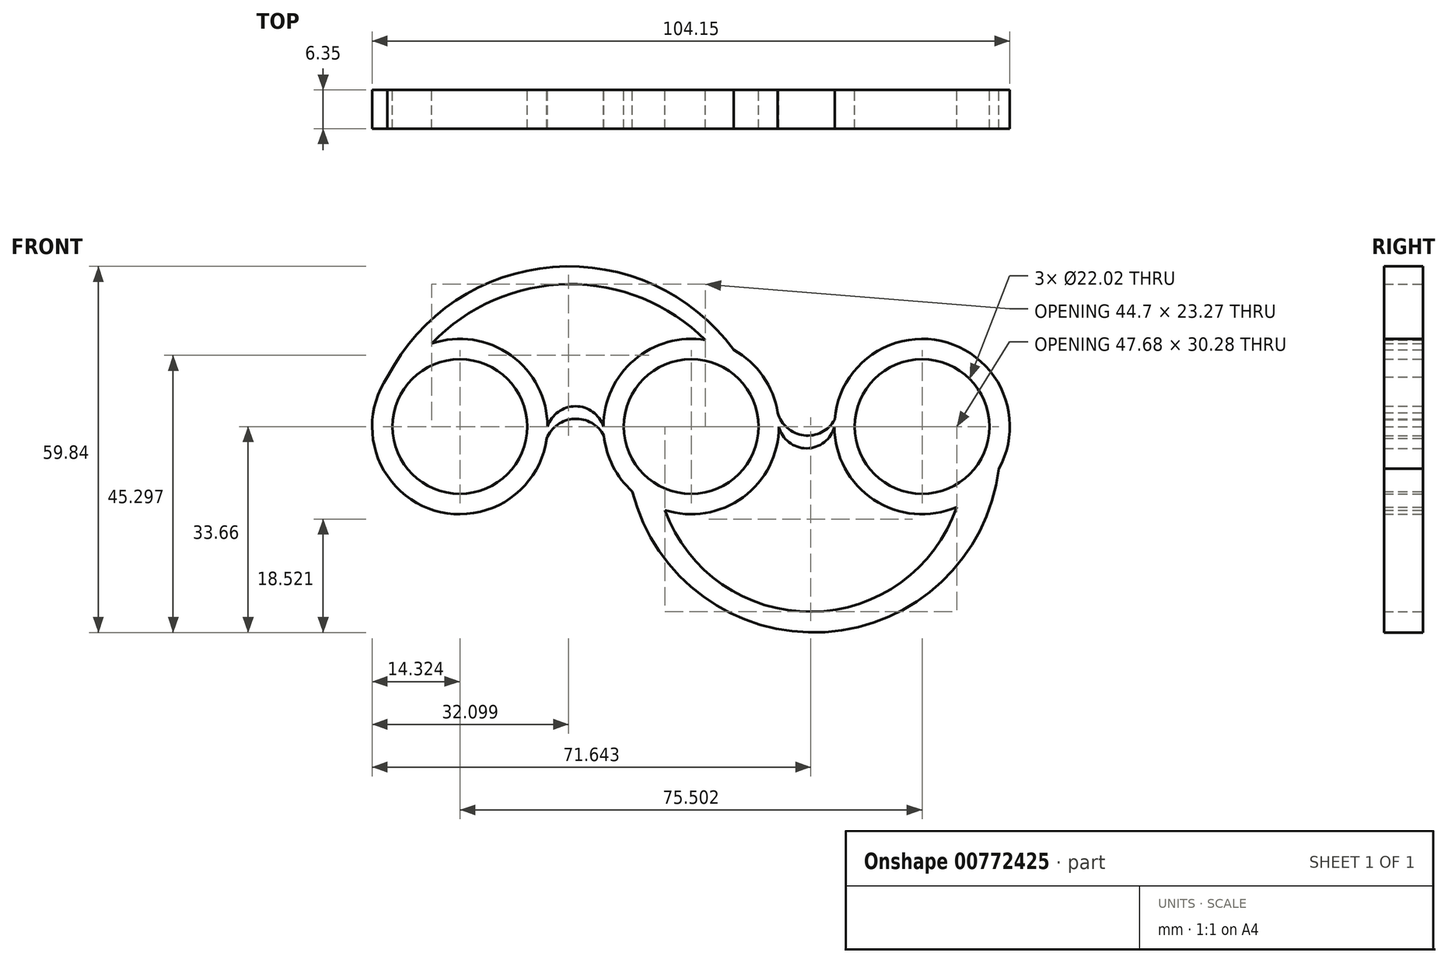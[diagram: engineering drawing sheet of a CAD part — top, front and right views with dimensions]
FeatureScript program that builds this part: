
annotation { "Feature Type Name" : "Feature", "Feature Type Description" : "" }
export const myFeature = defineFeature(function(context is Context, id is Id, definition is map)
    precondition{}
    {
        {
            var Q0;
            Q0=qCreatedBy(makeId("Front.planeOp"),FACE);
            var sketch = newSketch(context, id + "F0", { "sketchPlane" : qUnion([Q0])});
            skCircle(sketch, "E0", {"center": v(0, 0) * mm, "radius": 11.01 * mm});
            skCircle(sketch, "E1", {"center": v(37.72, 0) * mm, "radius": 11.01 * mm});
            skCircle(sketch, "E2", {"center": v(-37.79, 0) * mm, "radius": 11.01 * mm});
            skCircle(sketch, "E3", {"center": v(-37.79, 0) * mm, "radius": 14.33 * mm});
            skCircle(sketch, "E4", {"center": v(0, 0) * mm, "radius": 14.33 * mm});
            skCircle(sketch, "E5", {"center": v(37.72, 0) * mm, "radius": 14.33 * mm});
            skArc(sketch, "E6", {"start": v(-14.33, 0) * mm, "mid": v(-18.9, 3.32) * mm, "end": v(-23.46, 0) * mm});
            skArc(sketch, "E7", {"start": v(-14.25, -1.48) * mm, "mid": v(-19.07, 1.26) * mm, "end": v(-23.6, -1.95) * mm});
            skArc(sketch, "E8", {"start": v(14.33, 0) * mm, "mid": v(18.86, -3.56) * mm, "end": v(23.39, 0) * mm});
            skArc(sketch, "E9", {"start": v(14.15, 2.25) * mm, "mid": v(18.4, -1.44) * mm, "end": v(23.43, 1.1) * mm});
            skArc(sketch, "E10", {"start": v(6.94, 12.54) * mm, "mid": v(-22.58, 26.08) * mm, "end": v(-49.62, 8.08) * mm});
            skArc(sketch, "E11", {"start": v(2.34, 14.13) * mm, "mid": v(-20.13, 23.27) * mm, "end": v(-42.36, 13.58) * mm});
            skArc(sketch, "E12", {"start": v(-9.6, -10.63) * mm, "mid": v(21.9, -33.6) * mm, "end": v(50.28, -6.89) * mm});
            skArc(sketch, "E13", {"start": v(-4.3, -13.66) * mm, "mid": v(19.7, -30.28) * mm, "end": v(43.37, -13.16) * mm});
            skSolve(sketch);
        }
        {
            var Q0;
            Q0 = qSketchRegion(id + "F0", true);
            extrude(context, id + "F1", {"entities" : qUnion([Q0]), "depth" : 6.35 * mm, "offsetDistance" : 25.4 * mm});
        }
    });
